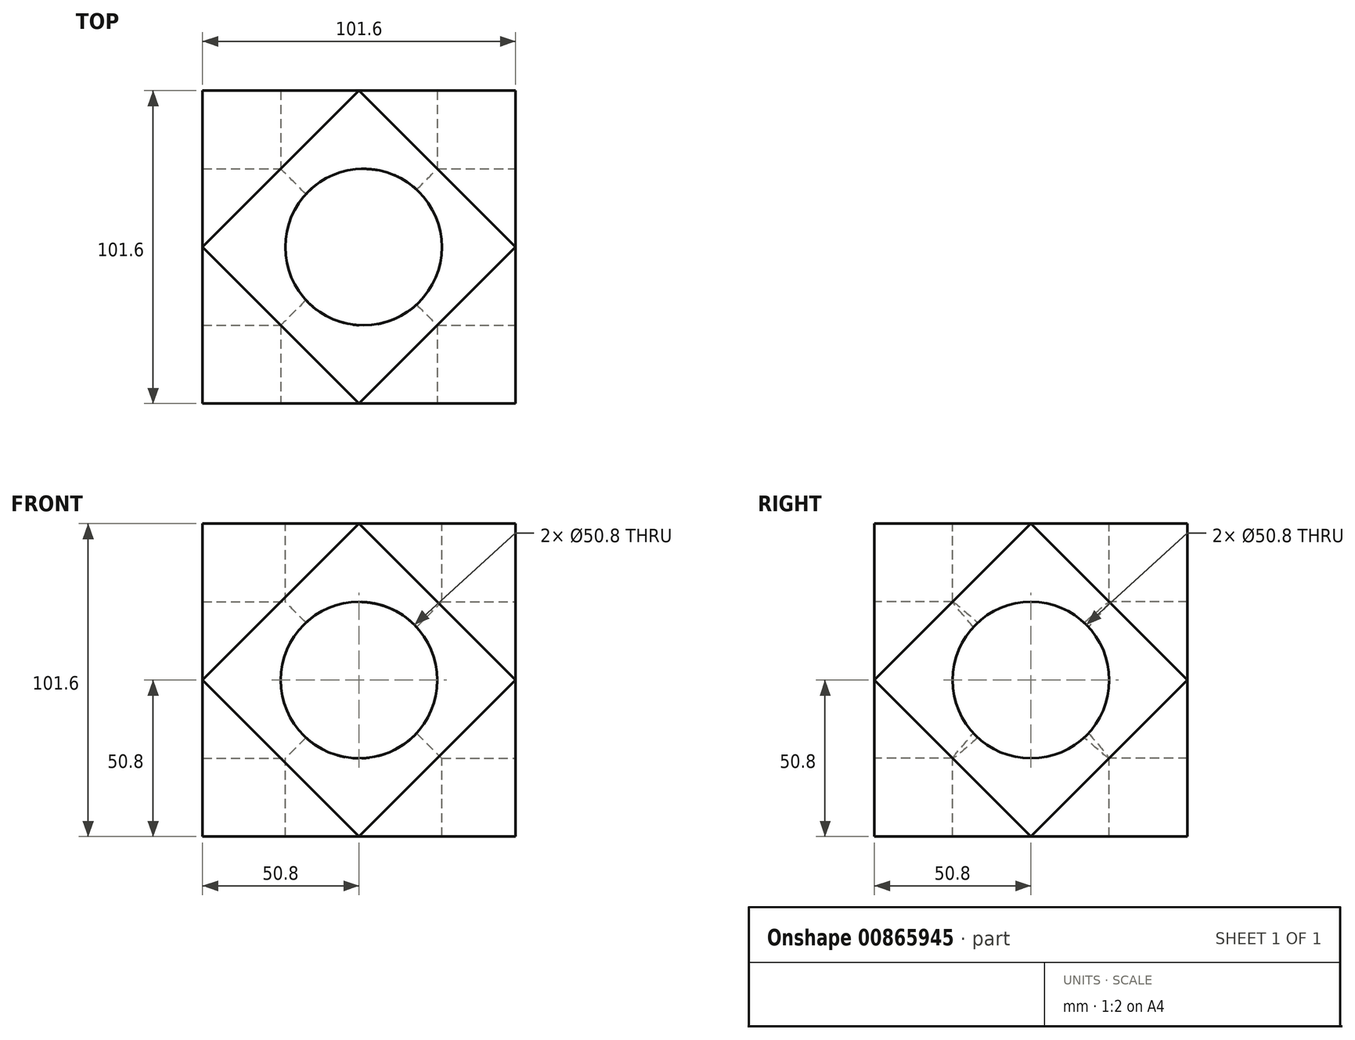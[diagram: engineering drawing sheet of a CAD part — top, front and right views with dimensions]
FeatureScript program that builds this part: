
annotation { "Feature Type Name" : "Feature", "Feature Type Description" : "" }
export const myFeature = defineFeature(function(context is Context, id is Id, definition is map)
    precondition{}
    {
        {
            var Q0;
            Q0=qCreatedBy(makeId("Top.planeOp"),FACE);
            var sketch = newSketch(context, id + "F0", { "sketchPlane" : qUnion([Q0])});
            skLineSegment(sketch, "E0.bottom", {"start": v(-50.8, 50.8) * mm, "end": v(50.8, 50.8) * mm});
            skLineSegment(sketch, "E0.top", {"start": v(-50.8, -50.8) * mm, "end": v(50.8, -50.8) * mm});
            skLineSegment(sketch, "E0.left", {"start": v(-50.8, 50.8) * mm, "end": v(-50.8, -50.8) * mm});
            skLineSegment(sketch, "E0.right", {"start": v(50.8, 50.8) * mm, "end": v(50.8, -50.8) * mm});
            skPoint(sketch, "E0.middle", {"position": v(0, 0) * mm});
            skSolve(sketch);
        }
        {
            var Q0;
            Q0 = qSketchRegion(id + "F0", true);
            extrude(context, id + "F1", {"entities" : qUnion([Q0]), "endBound" : BoundingType.SYMMETRIC, "depth" : 101.6 * mm, "offsetDistance" : 25.4 * mm});
        }
        {
            var Q0;
            Q0=makeQuery(id+"F1.opExtrude","CAP_FACE",FACE,{"disambiguationData":[OSD([sQuery(id+"F0.wireOp",EDGE,"E0.bottom"),sQuery(id+"F0.wireOp",EDGE,"E0.top"),sQuery(id+"F0.wireOp",EDGE,"E0.left"),sQuery(id+"F0.wireOp",EDGE,"E0.right")])],"isStart":false});
            var sketch = newSketch(context, id + "F2", { "sketchPlane" : qUnion([Q0])});
            skLineSegment(sketch, "E1", {"start": v(0, 50.8) * mm, "end": v(-50.8, 0) * mm});
            skLineSegment(sketch, "E2", {"start": v(-50.8, 0) * mm, "end": v(0, -50.8) * mm});
            skLineSegment(sketch, "E3", {"start": v(0, -50.8) * mm, "end": v(50.8, 0) * mm});
            skLineSegment(sketch, "E4", {"start": v(50.8, 0) * mm, "end": v(0, 50.8) * mm});
            skSolve(sketch);
        }
        {
            var Q0;
            Q0=makeQuery(id+"F1.opExtrude","SWEPT_FACE",FACE,{"disambiguationData":[OSD([sQuery(id+"F0.wireOp",EDGE,"E0.top")])]});
            var sketch = newSketch(context, id + "F3", { "sketchPlane" : qUnion([Q0])});
            skLineSegment(sketch, "E5", {"start": v(0, 50.8) * mm, "end": v(50.8, 0) * mm});
            skLineSegment(sketch, "E6", {"start": v(50.8, 0) * mm, "end": v(0, -50.8) * mm});
            skLineSegment(sketch, "E7", {"start": v(0, -50.8) * mm, "end": v(-50.8, 0) * mm});
            skLineSegment(sketch, "E8", {"start": v(-50.8, 0) * mm, "end": v(0, 50.8) * mm});
            skSolve(sketch);
        }
        {
            var Q0;
            Q0=sQuery(id+"F2.wireOp",EDGE,"E2");
            var Q1;
            Q1=sQuery(id+"F3.wireOp",EDGE,"E8");
            cPlane(context, id + "F4", {"entities" : qUnion([Q0, Q1]), "cplaneType" : CPlaneType.LINE_ANGLE, "offset" : 25.4 * mm, "angle" : 0 * degree, "width" : 152.4 * mm, "height" : 152.4 * mm});
        }
        {
            var Q0;
            Q0=makeQuery(id+"F1.opExtrude","SWEPT_FACE",FACE,{"disambiguationData":[OSD([sQuery(id+"F0.wireOp",EDGE,"E0.left")])]});
            var sketch = newSketch(context, id + "F5", { "sketchPlane" : qUnion([Q0])});
            skLineSegment(sketch, "E9", {"start": v(0, 50.8) * mm, "end": v(50.8, 0) * mm});
            skLineSegment(sketch, "E10", {"start": v(50.8, 0) * mm, "end": v(0, -50.8) * mm});
            skLineSegment(sketch, "E11", {"start": v(0, -50.8) * mm, "end": v(-50.8, 0) * mm});
            skLineSegment(sketch, "E12", {"start": v(-50.8, 0) * mm, "end": v(0, 50.8) * mm});
            skSolve(sketch);
        }
        {
            var Q0;
            Q0=qCreatedBy(id+"F4.planeOp",FACE);
            var sketch = newSketch(context, id + "F6", { "sketchPlane" : qUnion([Q0])});
            skLineSegment(sketch, "E13.bottom", {"start": v(-49.48, 53.57) * mm, "end": v(49.48, 53.57) * mm});
            skLineSegment(sketch, "E13.top", {"start": v(-49.48, -56.01) * mm, "end": v(49.48, -56.01) * mm});
            skLineSegment(sketch, "E13.left", {"start": v(-49.48, 53.57) * mm, "end": v(-49.48, -56.01) * mm});
            skLineSegment(sketch, "E13.right", {"start": v(49.48, 53.57) * mm, "end": v(49.48, -56.01) * mm});
            skPoint(sketch, "E13.middle", {"position": v(0, -1.22) * mm});
            skSolve(sketch);
        }
        {
            var Q0;
            Q0 = qSketchRegion(id + "F6", true);
            extrude(context, id + "F7", {"entities" : qUnion([Q0]), "operationType" : NewBodyOperationType.REMOVE, "endBound" : BoundingType.THROUGH_ALL, "depth" : 25.4 * mm, "offsetDistance" : 25.4 * mm});
        }
        {
            var Q0;
            Q0=sQuery(id+"F2.wireOp",EDGE,"E3");
            var Q1;
            Q1=sQuery(id+"F3.wireOp",EDGE,"E5");
            cPlane(context, id + "F8", {"entities" : qUnion([Q0, Q1]), "cplaneType" : CPlaneType.LINE_ANGLE, "offset" : 25.4 * mm, "angle" : 0 * degree, "width" : 152.4 * mm, "height" : 152.4 * mm});
        }
        {
            var Q0;
            Q0=qCreatedBy(id+"F8.planeOp",FACE);
            var sketch = newSketch(context, id + "F9", { "sketchPlane" : qUnion([Q0])});
            skCircle(sketch, "E14", {"center": v(-7.8, -7.12) * mm, "radius": 55.43 * mm});
            skSolve(sketch);
        }
        {
            var Q0;
            Q0 = qSketchRegion(id + "F9", true);
            extrude(context, id + "F10", {"entities" : qUnion([Q0]), "operationType" : NewBodyOperationType.REMOVE, "endBound" : BoundingType.THROUGH_ALL, "oppositeDirection" : true, "depth" : 25.4 * mm, "offsetDistance" : 25.4 * mm});
        }
        {
            var Q0;
            Q0=sQuery(id+"F5.wireOp",EDGE,"E12");
            var Q1;
            Q1=sQuery(id+"F2.wireOp",EDGE,"E1");
            cPlane(context, id + "F11", {"entities" : qUnion([Q0, Q1]), "cplaneType" : CPlaneType.LINE_ANGLE, "offset" : 25.4 * mm, "angle" : 0 * degree, "oppositeDirection" : true, "width" : 152.4 * mm, "height" : 152.4 * mm});
        }
        {
            var Q0;
            Q0=qCreatedBy(id+"F11.planeOp",FACE);
            var sketch = newSketch(context, id + "F12", { "sketchPlane" : qUnion([Q0])});
            skCircle(sketch, "E15", {"center": v(-13.3, -3.55) * mm, "radius": 66.86 * mm});
            skSolve(sketch);
        }
        {
            var Q0;
            Q0 = qSketchRegion(id + "F12", true);
            extrude(context, id + "F13", {"entities" : qUnion([Q0]), "operationType" : NewBodyOperationType.REMOVE, "endBound" : BoundingType.THROUGH_ALL, "oppositeDirection" : true, "depth" : 25.4 * mm, "offsetDistance" : 25.4 * mm});
        }
        {
            var Q0;
            Q0=sQuery(id+"F3.wireOp",EDGE,"E7");
            var Q1;
            Q1=sQuery(id+"F5.wireOp",EDGE,"E10");
            cPlane(context, id + "F14", {"entities" : qUnion([Q0, Q1]), "cplaneType" : CPlaneType.LINE_ANGLE, "offset" : 25.4 * mm, "angle" : 0 * degree, "width" : 152.4 * mm, "height" : 152.4 * mm});
        }
        {
            var Q0;
            Q0=qCreatedBy(id+"F14.planeOp",FACE);
            var sketch = newSketch(context, id + "F15", { "sketchPlane" : qUnion([Q0])});
            skCircle(sketch, "E16", {"center": v(-3.31, -3.84) * mm, "radius": 63.75 * mm});
            skSolve(sketch);
        }
        {
            var Q0;
            Q0=makeQuery(id+"F15.imprint","IMPRINT",FACE,{"disambiguationData":[TD([[makeQuery(id+"F15.imprint","IMPRINT",EDGE,{"derivedFrom":sQuery(id+"F15.wireOp",EDGE,"E16")}),1.0]])]});
            extrude(context, id + "F16", {"entities" : qUnion([Q0]), "operationType" : NewBodyOperationType.REMOVE, "endBound" : BoundingType.THROUGH_ALL, "depth" : 25.4 * mm, "offsetDistance" : 25.4 * mm});
        }
        {
            var Q0;
            Q0=makeQuery(id+"F1.opExtrude","SWEPT_FACE",FACE,{"disambiguationData":[OSD([sQuery(id+"F0.wireOp",EDGE,"E0.right")])]});
            var sketch = newSketch(context, id + "F17", { "sketchPlane" : qUnion([Q0])});
            skLineSegment(sketch, "E17", {"start": v(-50.8, 0) * mm, "end": v(0, -50.8) * mm});
            skLineSegment(sketch, "E18", {"start": v(0, -50.8) * mm, "end": v(50.8, 0) * mm});
            skLineSegment(sketch, "E19", {"start": v(50.8, 0) * mm, "end": v(0, 50.8) * mm});
            skSolve(sketch);
        }
        {
            var Q0;
            Q0=makeQuery(id+"F1.opExtrude","CAP_FACE",FACE,{"disambiguationData":[OSD([sQuery(id+"F0.wireOp",EDGE,"E0.bottom"),sQuery(id+"F0.wireOp",EDGE,"E0.top"),sQuery(id+"F0.wireOp",EDGE,"E0.left"),sQuery(id+"F0.wireOp",EDGE,"E0.right")])],"isStart":true});
            var sketch = newSketch(context, id + "F18", { "sketchPlane" : qUnion([Q0])});
            skLineSegment(sketch, "E20", {"start": v(0, 50.8) * mm, "end": v(50.8, 0) * mm});
            skLineSegment(sketch, "E21", {"start": v(50.8, 0) * mm, "end": v(0, -50.8) * mm});
            skLineSegment(sketch, "E22", {"start": v(0, -50.8) * mm, "end": v(-50.8, 0) * mm});
            skSolve(sketch);
        }
        {
            var Q0;
            Q0=makeQuery(id+"F1.opExtrude","SWEPT_FACE",FACE,{"disambiguationData":[OSD([sQuery(id+"F0.wireOp",EDGE,"E0.bottom")])]});
            var sketch = newSketch(context, id + "F19", { "sketchPlane" : qUnion([Q0])});
            skLineSegment(sketch, "E23", {"start": v(0, 50.8) * mm, "end": v(-50.8, 0) * mm});
            skLineSegment(sketch, "E24", {"start": v(-50.8, 0) * mm, "end": v(0, -50.8) * mm});
            skLineSegment(sketch, "E25", {"start": v(0, -50.8) * mm, "end": v(50.8, 0) * mm});
            skSolve(sketch);
        }
        {
            var Q0;
            Q0=sQuery(id+"F2.wireOp",EDGE,"E4");
            var Q1;
            Q1=sQuery(id+"F19.wireOp",EDGE,"E23");
            cPlane(context, id + "F20", {"entities" : qUnion([Q0, Q1]), "cplaneType" : CPlaneType.LINE_ANGLE, "offset" : 25.4 * mm, "angle" : 0 * degree, "oppositeDirection" : true, "width" : 152.4 * mm, "height" : 152.4 * mm});
        }
        {
            var Q0;
            Q0=qCreatedBy(id+"F20.planeOp",FACE);
            var sketch = newSketch(context, id + "F21", { "sketchPlane" : qUnion([Q0])});
            skCircle(sketch, "E26", {"center": v(0, -4.45) * mm, "radius": 117.8 * mm});
            skSolve(sketch);
        }
        {
            var Q0;
            Q0 = qSketchRegion(id + "F21", true);
            extrude(context, id + "F22", {"entities" : qUnion([Q0]), "operationType" : NewBodyOperationType.REMOVE, "endBound" : BoundingType.THROUGH_ALL, "oppositeDirection" : true, "depth" : 25.4 * mm, "offsetDistance" : 25.4 * mm});
        }
        {
            var Q0;
            Q0=sQuery(id+"F18.wireOp",EDGE,"E21");
            var Q1;
            Q1=sQuery(id+"F17.wireOp",EDGE,"E18");
            cPlane(context, id + "F23", {"entities" : qUnion([Q0, Q1]), "cplaneType" : CPlaneType.LINE_ANGLE, "offset" : 25.4 * mm, "angle" : 0 * degree, "width" : 152.4 * mm, "height" : 152.4 * mm});
        }
        {
            var Q0;
            Q0=qCreatedBy(id+"F23.planeOp",FACE);
            var sketch = newSketch(context, id + "F24", { "sketchPlane" : qUnion([Q0])});
            skCircle(sketch, "E27", {"center": v(-11.08, -8.17) * mm, "radius": 77.2 * mm});
            skSolve(sketch);
        }
        {
            var Q0;
            Q0 = qSketchRegion(id + "F24", true);
            extrude(context, id + "F25", {"entities" : qUnion([Q0]), "operationType" : NewBodyOperationType.REMOVE, "endBound" : BoundingType.THROUGH_ALL, "depth" : 25.4 * mm, "offsetDistance" : 25.4 * mm});
        }
        {
            var Q0;
            Q0=sQuery(id+"F17.wireOp",EDGE,"E17");
            var Q1;
            Q1=sQuery(id+"F3.wireOp",EDGE,"E6");
            cPlane(context, id + "F26", {"entities" : qUnion([Q0, Q1]), "cplaneType" : CPlaneType.LINE_ANGLE, "offset" : 25.4 * mm, "angle" : 0 * degree, "width" : 152.4 * mm, "height" : 152.4 * mm});
        }
        {
            var Q0;
            Q0=qCreatedBy(id+"F26.planeOp",FACE);
            var sketch = newSketch(context, id + "F27", { "sketchPlane" : qUnion([Q0])});
            skCircle(sketch, "E28", {"center": v(0, -3.75) * mm, "radius": 77.6 * mm});
            skSolve(sketch);
        }
        {
            var Q0;
            Q0 = qSketchRegion(id + "F27", true);
            extrude(context, id + "F28", {"entities" : qUnion([Q0]), "operationType" : NewBodyOperationType.REMOVE, "endBound" : BoundingType.THROUGH_ALL, "oppositeDirection" : true, "depth" : 25.4 * mm, "offsetDistance" : 25.4 * mm});
        }
        {
            var Q0;
            Q0=sQuery(id+"F5.wireOp",EDGE,"E11");
            var Q1;
            Q1=sQuery(id+"F19.wireOp",EDGE,"E25");
            cPlane(context, id + "F29", {"entities" : qUnion([Q0, Q1]), "cplaneType" : CPlaneType.LINE_ANGLE, "offset" : 25.4 * mm, "angle" : 0 * degree, "width" : 152.4 * mm, "height" : 152.4 * mm});
        }
        {
            var Q0;
            Q0=qCreatedBy(id+"F29.planeOp",FACE);
            var sketch = newSketch(context, id + "F30", { "sketchPlane" : qUnion([Q0])});
            skCircle(sketch, "E29", {"center": v(-6.14, -7.86) * mm, "radius": 68.12 * mm});
            skSolve(sketch);
        }
        {
            var Q0;
            Q0 = qSketchRegion(id + "F30", true);
            extrude(context, id + "F31", {"entities" : qUnion([Q0]), "operationType" : NewBodyOperationType.REMOVE, "endBound" : BoundingType.THROUGH_ALL, "oppositeDirection" : true, "depth" : 25.4 * mm, "offsetDistance" : 25.4 * mm});
        }
        {
            var Q0;
            Q0=makeQuery(id+"F2.imprint","IMPRINT",FACE,{"disambiguationData":[TD([[makeQuery(id+"F2.imprint","IMPRINT",EDGE,{"derivedFrom":sQuery(id+"F2.wireOp",EDGE,"E1")}),1.0]])]});
            var sketch = newSketch(context, id + "F32", { "sketchPlane" : qUnion([Q0])});
            skCircle(sketch, "E30", {"center": v(1.46, 0) * mm, "radius": 25.4 * mm});
            skSolve(sketch);
        }
        {
            var Q0;
            Q0 = qSketchRegion(id + "F32", true);
            extrude(context, id + "F33", {"entities" : qUnion([Q0]), "operationType" : NewBodyOperationType.REMOVE, "endBound" : BoundingType.THROUGH_ALL, "oppositeDirection" : true, "depth" : 25.4 * mm, "offsetDistance" : 25.4 * mm});
        }
        {
            var Q0;
            Q0=makeQuery(id+"F3.imprint","IMPRINT",FACE,{"disambiguationData":[TD([[makeQuery(id+"F3.imprint","IMPRINT",EDGE,{"derivedFrom":sQuery(id+"F3.wireOp",EDGE,"E5")}),-1.0]])]});
            var sketch = newSketch(context, id + "F34", { "sketchPlane" : qUnion([Q0])});
            skCircle(sketch, "E31", {"center": v(0, 0) * mm, "radius": 25.4 * mm});
            skSolve(sketch);
        }
        {
            var Q0;
            Q0 = qSketchRegion(id + "F34", true);
            extrude(context, id + "F35", {"entities" : qUnion([Q0]), "operationType" : NewBodyOperationType.REMOVE, "endBound" : BoundingType.THROUGH_ALL, "oppositeDirection" : true, "depth" : 25.4 * mm, "offsetDistance" : 25.4 * mm});
        }
        {
            var Q0;
            Q0=makeQuery(id+"F17.imprint","IMPRINT",FACE,{"disambiguationData":[TD([[makeQuery(id+"F17.imprint","IMPRINT",EDGE,{"derivedFrom":sQuery(id+"F17.wireOp",EDGE,"E17")}),1.0]])]});
            var sketch = newSketch(context, id + "F36", { "sketchPlane" : qUnion([Q0])});
            skCircle(sketch, "E32", {"center": v(0, 0) * mm, "radius": 25.4 * mm});
            skSolve(sketch);
        }
        {
            var Q0;
            Q0 = qSketchRegion(id + "F36", true);
            extrude(context, id + "F37", {"entities" : qUnion([Q0]), "operationType" : NewBodyOperationType.REMOVE, "endBound" : BoundingType.THROUGH_ALL, "oppositeDirection" : true, "depth" : 25.4 * mm, "offsetDistance" : 25.4 * mm});
        }
    });
